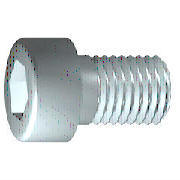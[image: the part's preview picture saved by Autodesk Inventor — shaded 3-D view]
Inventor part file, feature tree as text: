
AUTODESK INVENTOR PART (.ipt)
format: ipt  version: 2022 (Build 260153000, 153)  size: 196,096 bytes
history: native  units: mm (DEFAULTED — no unit token found)
features: sketch x2, other x1, extrude x1, plane x1, fillet x1
ambient origin geometry x7: Origin, YZ Plane, XY Plane, X Axis, Y Axis, Z Axis, Center Point
bodies: Solid1 (feature_tree)
feature tree (6):
  other  "Базовый элемент"
  extrude  "Паз"  Depth=6.65mm
  plane  "Work Plane1"
  fillet  "Fillet2"  Radius=0.276153mm
  sketch  "Эскиз1"
  sketch  "Эскиз2"
